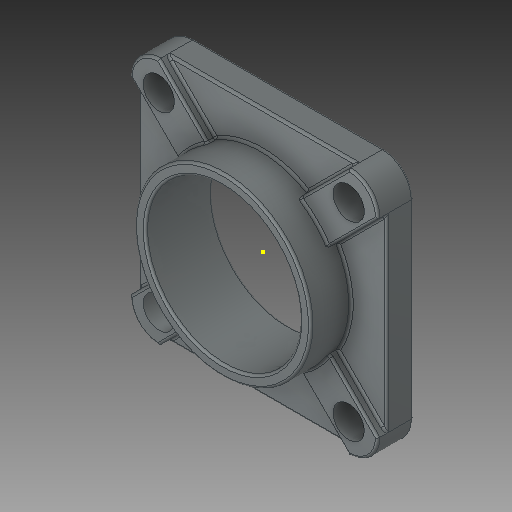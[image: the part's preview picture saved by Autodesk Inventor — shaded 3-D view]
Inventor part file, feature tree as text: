
AUTODESK INVENTOR PART (.ipt)
format: ipt  version: 2019 (Build 230136000, 136)  size: 483,840 bytes
history: native  units: in
note: dims shown in document units (in); Inventor stores cm internally (conversion verified against a paired STEP export)
features: sketch x10, other x3
ambient origin geometry x8: Origin, YZ Plane, XZ Plane, XY Plane, X Axis, Y Axis, Z Axis, Center Point
bodies: Solid1 (feature_tree)
feature tree (13):
  other  "project flange bearing part1_MIR5.ipt"
  other  "Solid1::project flange bearing part1_MIR5.ipt"
  other  "TaggingFeature1"
  sketch  "Sketch1"  dims[d0=0.3937in]
  sketch  "Sketch2"
  sketch  "Sketch3"
  sketch  "Sketch4"
  sketch  "Sketch5"
  sketch  "Sketch6"
  sketch  "Sketch7"
  sketch  "Sketch8"
  sketch  "Sketch9"
  sketch  "Sketch10"
